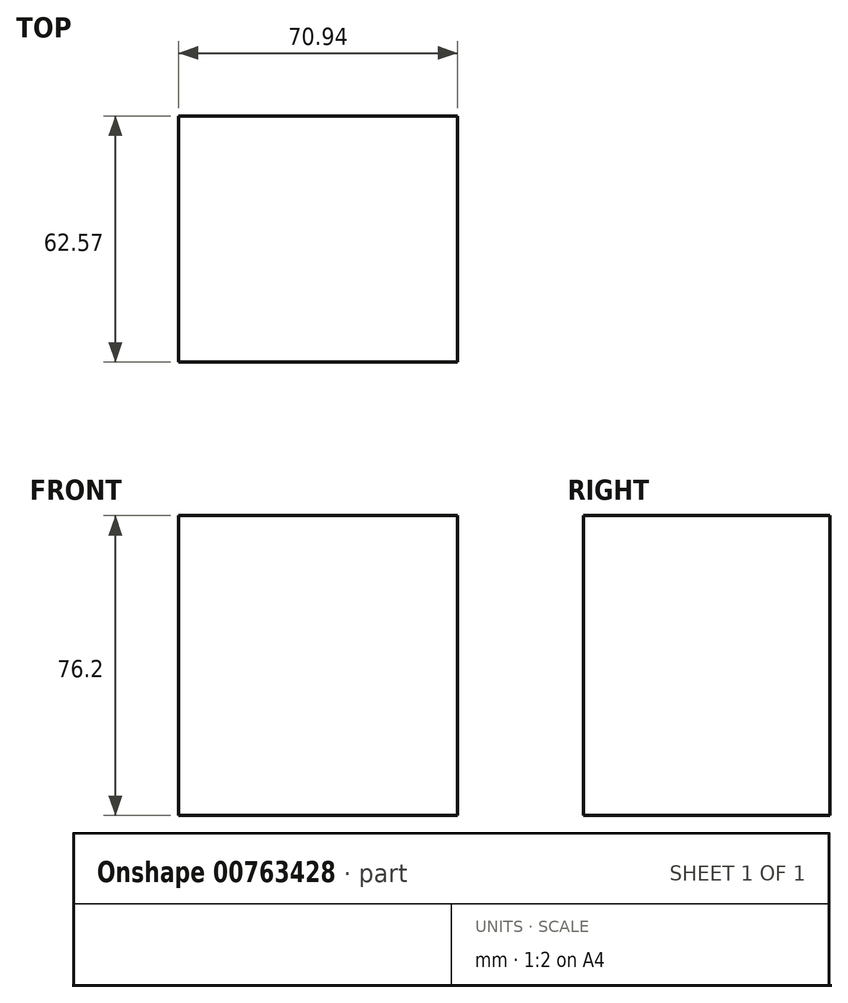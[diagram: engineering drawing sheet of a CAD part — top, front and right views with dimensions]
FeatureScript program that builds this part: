
annotation { "Feature Type Name" : "Feature", "Feature Type Description" : "" }
export const myFeature = defineFeature(function(context is Context, id is Id, definition is map)
    precondition{}
    {
        {
            var Q0;
            Q0=qCreatedBy(makeId("Top.planeOp"),FACE);
            var sketch = newSketch(context, id + "F0", { "sketchPlane" : qUnion([Q0])});
            skLineSegment(sketch, "E0.bottom", {"start": v(35.47, -40.15) * mm, "end": v(-35.47, -40.15) * mm});
            skLineSegment(sketch, "E0.top", {"start": v(35.47, 22.42) * mm, "end": v(-35.47, 22.42) * mm});
            skLineSegment(sketch, "E0.left", {"start": v(35.47, -40.15) * mm, "end": v(35.47, 22.42) * mm});
            skLineSegment(sketch, "E0.right", {"start": v(-35.47, -40.15) * mm, "end": v(-35.47, 22.42) * mm});
            skPoint(sketch, "E0.middle", {"position": v(0, -8.87) * mm});
            skSolve(sketch);
        }
        {
            var Q0;
            Q0 = qSketchRegion(id + "F0", true);
            extrude(context, id + "F1", {"entities" : qUnion([Q0]), "depth" : 76.2 * mm, "offsetDistance" : 25.4 * mm});
        }
    });
